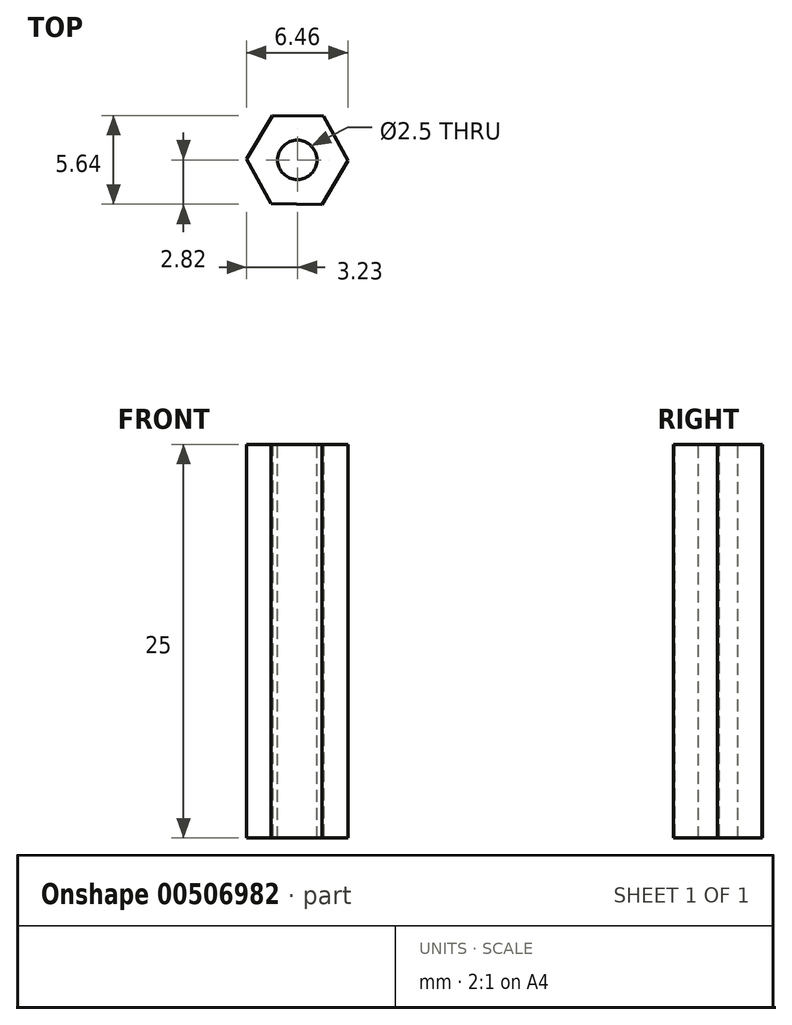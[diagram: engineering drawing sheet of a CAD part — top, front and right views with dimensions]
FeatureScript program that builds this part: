
annotation { "Feature Type Name" : "Feature", "Feature Type Description" : "" }
export const myFeature = defineFeature(function(context is Context, id is Id, definition is map)
    precondition{}
    {
        {
            var Q0;
            Q0=qCreatedBy(makeId("Top.planeOp"),FACE);
            var sketch = newSketch(context, id + "F0", { "sketchPlane" : qUnion([Q0])});
            skCircle(sketch, "E0.cCircle", {"center": v(0, 0) * mm, "radius": 2.8 * mm, "construction": true});
            skLineSegment(sketch, "E0.0", {"start": v(3.23, -0.05) * mm, "end": v(1.57, -2.82) * mm});
            skLineSegment(sketch, "E0.1", {"start": v(1.57, -2.82) * mm, "end": v(-1.66, -2.78) * mm});
            skLineSegment(sketch, "E0.2", {"start": v(-1.66, -2.78) * mm, "end": v(-3.23, 0.05) * mm});
            skLineSegment(sketch, "E0.3", {"start": v(-3.23, 0.05) * mm, "end": v(-1.57, 2.82) * mm});
            skLineSegment(sketch, "E0.4", {"start": v(-1.57, 2.82) * mm, "end": v(1.66, 2.78) * mm});
            skLineSegment(sketch, "E0.5", {"start": v(1.66, 2.78) * mm, "end": v(3.23, -0.05) * mm});
            skPoint(sketch, "E0.0.midPoint", {"position": v(2.4, -1.44) * mm});
            skSolve(sketch);
        }
        {
            var Q0;
            Q0=makeQuery(id+"F0.imprint","IMPRINT",FACE,{"disambiguationData":[TD([[makeQuery(id+"F0.imprint","IMPRINT",EDGE,{"derivedFrom":sQuery(id+"F0.wireOp",EDGE,"E0.0")}),-1.0]])]});
            extrude(context, id + "F1", {"entities" : qUnion([Q0]), "depth" : 25 * mm, "offsetDistance" : 25 * mm});
        }
        {
            var Q0;
            Q0=makeQuery(id+"F1.opExtrude","CAP_FACE",FACE,{"disambiguationData":[OSD([sQuery(id+"F0.wireOp",EDGE,"E0.0"),sQuery(id+"F0.wireOp",EDGE,"E0.1"),sQuery(id+"F0.wireOp",EDGE,"E0.2"),sQuery(id+"F0.wireOp",EDGE,"E0.3"),sQuery(id+"F0.wireOp",EDGE,"E0.4"),sQuery(id+"F0.wireOp",EDGE,"E0.5")])],"isStart":false});
            var sketch = newSketch(context, id + "F2", { "sketchPlane" : qUnion([Q0])});
            skPoint(sketch, "E1.0", {"position": v(0, 0) * mm});
            skSolve(sketch);
        }
        {
            var Q0;
            Q0=sQuery(id+"F2.wireOp",VERTEX,"E1.0");
            var Q1;
            Q1=makeQuery(id+"F1.opExtrude","SWEPT_BODY",BODY,{"disambiguationData":[OSD([sQuery(id+"F0.wireOp",EDGE,"E0.0"),sQuery(id+"F0.wireOp",EDGE,"E0.1"),sQuery(id+"F0.wireOp",EDGE,"E0.2"),sQuery(id+"F0.wireOp",EDGE,"E0.3"),sQuery(id+"F0.wireOp",EDGE,"E0.4"),sQuery(id+"F0.wireOp",EDGE,"E0.5")])]});
            hole(context, id + "F3", {"style" : HoleStyle.SIMPLE, "endStyle" : HoleEndStyle.THROUGH, "standardTappedOrClearance" : lookupTablePath({ "standard" : "ISO", "engagement" : "75%", "pitch" : "0.5 mm", "size" : "M3", "type" : "Tapped" }), "standardBlindInLast" : lookupTablePath({ "standard" : "ISO", "engagement" : "75%", "pitch" : "0.5 mm", "size" : "M3", "type" : "Tapped" }), "holeDiameter" : 2.5 * mm, "showTappedDepth" : true, "isTappedThrough" : true, "tappedDepth" : 12 * mm, "tapClearance" : 3, "startFromSketch" : true, "locations" : qUnion([Q0]), "scope" : qUnion([Q1]), "majorDiameter" : 3 * mm});
        }
    });
